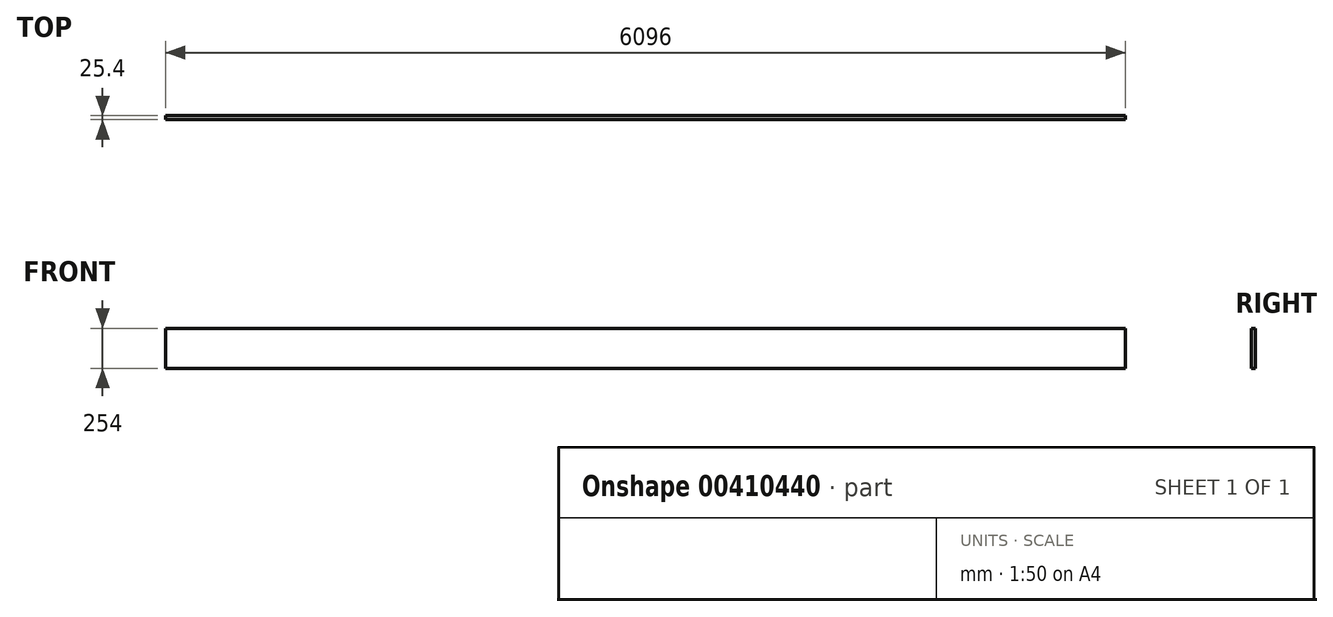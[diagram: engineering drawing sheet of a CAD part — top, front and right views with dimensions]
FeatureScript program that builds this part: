
annotation { "Feature Type Name" : "Feature", "Feature Type Description" : "" }
export const myFeature = defineFeature(function(context is Context, id is Id, definition is map)
    precondition{}
    {
        {
            var Q0;
            Q0=qCreatedBy(makeId("Front.planeOp"),FACE);
            var sketch = newSketch(context, id + "F0", { "sketchPlane" : qUnion([Q0])});
            skLineSegment(sketch, "E0.bottom", {"start": v(-3048, 127) * mm, "end": v(3048, 127) * mm});
            skLineSegment(sketch, "E0.top", {"start": v(-3048, -127) * mm, "end": v(3048, -127) * mm});
            skLineSegment(sketch, "E0.left", {"start": v(-3048, 127) * mm, "end": v(-3048, -127) * mm});
            skLineSegment(sketch, "E0.right", {"start": v(3048, 127) * mm, "end": v(3048, -127) * mm});
            skPoint(sketch, "E0.middle", {"position": v(0, 0) * mm});
            skSolve(sketch);
        }
        {
            var Q0;
            Q0 = qSketchRegion(id + "F0", true);
            extrude(context, id + "F1", {"entities" : qUnion([Q0]), "depth" : 25.4 * mm, "offsetDistance" : 25.4 * mm});
        }
    });
